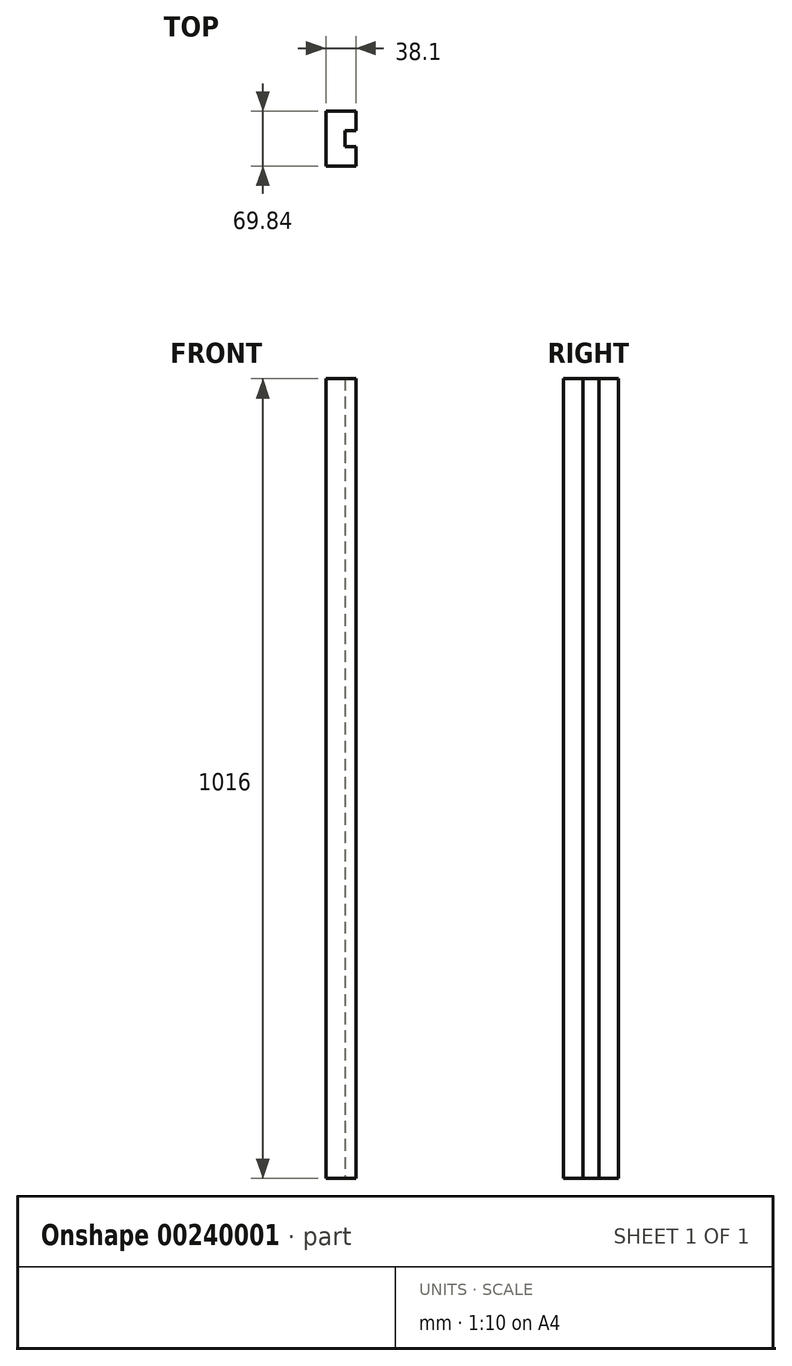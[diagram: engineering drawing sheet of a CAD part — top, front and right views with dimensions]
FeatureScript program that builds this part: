
annotation { "Feature Type Name" : "Feature", "Feature Type Description" : "" }
export const myFeature = defineFeature(function(context is Context, id is Id, definition is map)
    precondition{}
    {
        {
            var Q0;
            Q0=qCreatedBy(makeId("Top.planeOp"),FACE);
            var sketch = newSketch(context, id + "F0", { "sketchPlane" : qUnion([Q0])});
            skLineSegment(sketch, "E0", {"start": v(-38.1, -34.93) * mm, "end": v(-38.1, -10.32) * mm});
            skLineSegment(sketch, "E1", {"start": v(-38.1, -10.32) * mm, "end": v(-24.6, -10.32) * mm});
            skLineSegment(sketch, "E2", {"start": v(-24.6, -10.32) * mm, "end": v(-24.6, 10.32) * mm});
            skLineSegment(sketch, "E3", {"start": v(-24.6, 10.32) * mm, "end": v(-38.1, 10.32) * mm});
            skLineSegment(sketch, "E4", {"start": v(-38.1, 10.32) * mm, "end": v(-38.1, 34.92) * mm});
            skLineSegment(sketch, "E5", {"start": v(-38.1, 34.92) * mm, "end": v(38.1, 34.92) * mm});
            skLineSegment(sketch, "E6", {"start": v(38.1, 34.92) * mm, "end": v(38.1, 10.32) * mm});
            skLineSegment(sketch, "E7", {"start": v(38.1, 10.32) * mm, "end": v(24.6, 10.32) * mm});
            skLineSegment(sketch, "E8", {"start": v(24.6, 10.32) * mm, "end": v(24.6, -10.32) * mm});
            skLineSegment(sketch, "E9", {"start": v(24.6, -10.32) * mm, "end": v(38.1, -10.32) * mm});
            skLineSegment(sketch, "E10", {"start": v(38.1, -10.32) * mm, "end": v(38.1, -34.93) * mm});
            skLineSegment(sketch, "E11", {"start": v(38.1, -34.93) * mm, "end": v(-38.1, -34.93) * mm});
            skLineSegment(sketch, "E12", {"start": v(38.1, 34.93) * mm, "end": v(-38.1, -34.93) * mm, "construction": true});
            skLineSegment(sketch, "E13", {"start": v(-38.1, 34.93) * mm, "end": v(38.1, -34.93) * mm, "construction": true});
            skPoint(sketch, "E14", {"position": v(0, 0) * mm});
            skLineSegment(sketch, "E15", {"start": v(0, -34.93) * mm, "end": v(0, 34.92) * mm});
            skSolve(sketch);
        }
        {
            var Q0;
            {var subQ0=sQuery(id+"F0.wireOp",EDGE,"E6");Q0=makeQuery(id+"F0.imprint","IMPRINT",FACE,{"disambiguationData":[TD([[makeQuery(id+"F0.imprint","IMPRINT",EDGE,{"derivedFrom":subQ0}),-1.0]])]});}
            extrude(context, id + "F1", {"entities" : qUnion([Q0]), "depth" : 1016 * mm, "offsetDistance" : 25.4 * mm});
        }
    });
